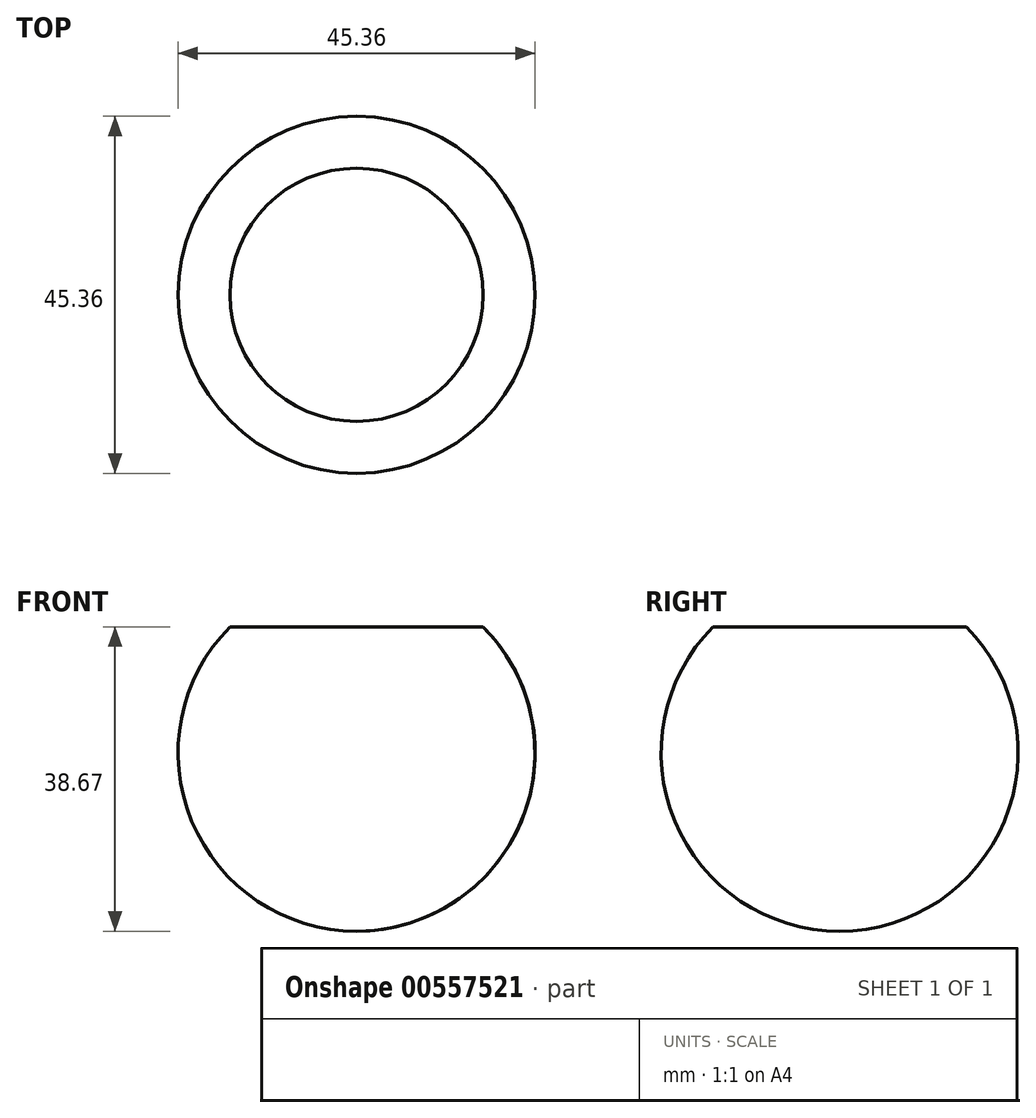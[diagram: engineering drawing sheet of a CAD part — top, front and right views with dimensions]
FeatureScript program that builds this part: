
annotation { "Feature Type Name" : "Feature", "Feature Type Description" : "" }
export const myFeature = defineFeature(function(context is Context, id is Id, definition is map)
    precondition{}
    {
        {
            var Q0;
            Q0=qCreatedBy(makeId("Front.planeOp"),FACE);
            var sketch = newSketch(context, id + "F0", { "sketchPlane" : qUnion([Q0])});
            skArc(sketch, "E0", {"start": v(0, -22.68) * mm, "mid": v(22.68, 0) * mm, "end": v(0, 22.68) * mm});
            skLineSegment(sketch, "E1", {"start": v(0, 22.68) * mm, "end": v(0, -22.68) * mm});
            skLineSegment(sketch, "E2", {"start": v(0, 36.12) * mm, "end": v(0, -34.64) * mm, "construction": true});
            skSolve(sketch);
        }
        {
            var Q0;
            Q0 = qSketchRegion(id + "F0", true);
            var Q1;
            Q1=sQuery(id+"F0.wireOp",EDGE,"E2");
            revolve(context, id + "F1", {"entities" : qUnion([Q0]), "axis" : qUnion([Q1]), "revolveType" : RevolveType.FULL});
        }
        {
            var Q0;
            Q0=qCreatedBy(makeId("Front.planeOp"),FACE);
            var sketch = newSketch(context, id + "F2", { "sketchPlane" : qUnion([Q0])});
            skLineSegment(sketch, "E3.bottom", {"start": v(-22.35, 29.9) * mm, "end": v(22.94, 29.9) * mm});
            skLineSegment(sketch, "E3.top", {"start": v(-22.35, 15.99) * mm, "end": v(22.94, 15.99) * mm});
            skLineSegment(sketch, "E3.left", {"start": v(-22.35, 29.9) * mm, "end": v(-22.35, 15.99) * mm});
            skLineSegment(sketch, "E3.right", {"start": v(22.94, 29.9) * mm, "end": v(22.94, 15.99) * mm});
            skSolve(sketch);
        }
        {
            var Q0;
            Q0 = qSketchRegion(id + "F2", true);
            extrude(context, id + "F3", {"entities" : qUnion([Q0]), "operationType" : NewBodyOperationType.REMOVE, "endBound" : BoundingType.SYMMETRIC, "depth" : 50 * mm, "offsetDistance" : 25 * mm});
        }
    });
